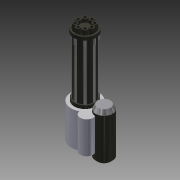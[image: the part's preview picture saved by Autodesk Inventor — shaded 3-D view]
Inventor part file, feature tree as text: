
AUTODESK INVENTOR PART (.ipt)
format: ipt  version: 2014 (Build 180170000, 170)  size: 495,104 bytes
history: native  units: in
note: dims shown in document units (in); Inventor stores cm internally (conversion verified against a paired STEP export)
features: sketch x24, extrude x22, loft x3, other x3, plane x2
ambient origin geometry x8: Origin, YZ Plane, XZ Plane, XY Plane, X Axis, Y Axis, Z Axis, Center Point
bodies: Solid1 (feature_tree)
feature tree (54):
  extrude  "Extrusion1"  Depth=1.5in TaperAngle=0.0deg
  extrude  "Extrusion2"  Depth=4.0in TaperAngle=0.0deg
  extrude  "Extrusion4"  Depth=6.5in
  extrude  "Extrusion5"  Depth=2.25in
  extrude  "Extrusion6"  Depth=2.25in
  extrude  "Extrusion8"  Depth=1.25in
  extrude  "Extrusion9"  Depth=1.25in
  extrude  "Extrusion10"  Depth=1.25in
  extrude  "Extrusion11"  Depth=1.25in
  sketch  "Sketch12"  dims[d24=1.25in d25=1.25in]
  sketch  "Sketch13"  dims[d26=1.25in d27=3.0in d28=0.0in]
  sketch  "Sketch14"  dims[d30=27.5591in d31=0.0in d32=10.0in]
  sketch  "Sketch15"  dims[d33=1.0in d34=0.5in d35=0.0in d36=0.0in d37=8.75in]
  sketch  "Sketch16"  dims[d40=10.5in d41=9.0in]
  sketch  "Sketch17"  dims[d53=3.0in d54=0.0in d55=26.6in d56=0.0in]
  extrude  "Extrusion12"  Depth=3.0in TaperAngle=0.0deg
  extrude  "Extrusion13"  Depth=10.0in
  extrude  "Extrusion14"  Depth=1.0in
  extrude  "Extrusion15"  Depth=9.0in
  extrude  "Extrusion16"  Depth=3.0in TaperAngle=0.0deg
  extrude  "Extrusion17"  Depth=0.183in
  extrude  "Extrusion22"  Depth=23.6in TaperAngle=0.0deg
  sketch  "Sketch26"  dims[d60=0.183in d61=23.6in d62=0.0in]
  loft  "Loft3"
  extrude  "Extrusion23"  Depth=0.183in
  extrude  "Extrusion25"  Depth=0.183in
  plane  "Work Plane6"
  loft  "Loft5"
  plane  "Work Plane7"
  loft  "Loft6"
  extrude  "Extrusion26"  Depth=23.6in TaperAngle=0.0deg
  extrude  "Extrusion27"  Depth=23.6in TaperAngle=0.0deg
  extrude  "Extrusion28"  Depth=1.5in
  extrude  "Extrusion29"  Depth=1.0in
  sketch  "Sketch1"  dims[d3=1.5in d4=0.0in d5=0.5in d6=0.0in]
  sketch  "Sketch3"  dims[d9=4.0in d10=1.75in d11=0.0in]
  sketch  "Sketch4"  dims[d12=6.5in d13=2.25in]
  sketch  "Sketch5"  dims[d14=2.25in d15=2.25in]
  sketch  "Sketch8"  dims[d16=2.25in d17=2.25in]
  sketch  "Sketch9"  dims[d18=2.25in d19=1.25in]
  sketch  "Sketch10"  dims[d20=1.25in d21=1.25in]
  sketch  "Sketch11"  dims[d22=1.25in d23=1.25in]
  sketch  "Sketch25"  dims[d57=23.6in d58=0.0in d59=0.183in]
  other  "Edges2"
  sketch  "Sketch28"  dims[d63=0.183in d64=0.183in]
  sketch  "Sketch33"  dims[d65=0.183in d66=0.183in]
  sketch  "Sketch35"  dims[d67=0.183in d68=0.183in]
  other  "Edges4"
  sketch  "Sketch36"  dims[d69=0.183in d70=0.183in]
  other  "Edges5"
  sketch  "Sketch37"  dims[d71=0.183in d72=23.6in d73=0.0in]
  sketch  "Sketch38"  dims[d74=23.6in d75=0.0in d76=23.6in d77=0.0in]
  sketch  "Sketch39"  dims[d78=23.6in d79=0.0in d80=23.6in d81=0.0in]
  sketch  "Sketch40"  dims[d82=23.6in d83=0.0in d115=1.5in d116=0.5497in d117=1.5in d118=0.6871in d119=0.5in d120=0.0in d121=2.0in d122=0.0in d123=90.0deg d124=0.0in d125=90.0deg d126=13.0in d127=16.0in d128=0.0in d135=2.0in d136=17.0in d137=0.0in d138=0.0in d145=2.0in d146=6.0in d147=0.0in d148=90.0deg d149=0.0in d150=90.0deg d151=1.0in d152=6.0in d153=0.0in d154=90.0deg d155=0.0in d156=90.0deg d157=10.0in d158=1.0in d159=0.0in d160=6.0in d161=16.0in d162=0.0in d163=1.0in d164=0.0in d165=1.0in d166=0.0in]
